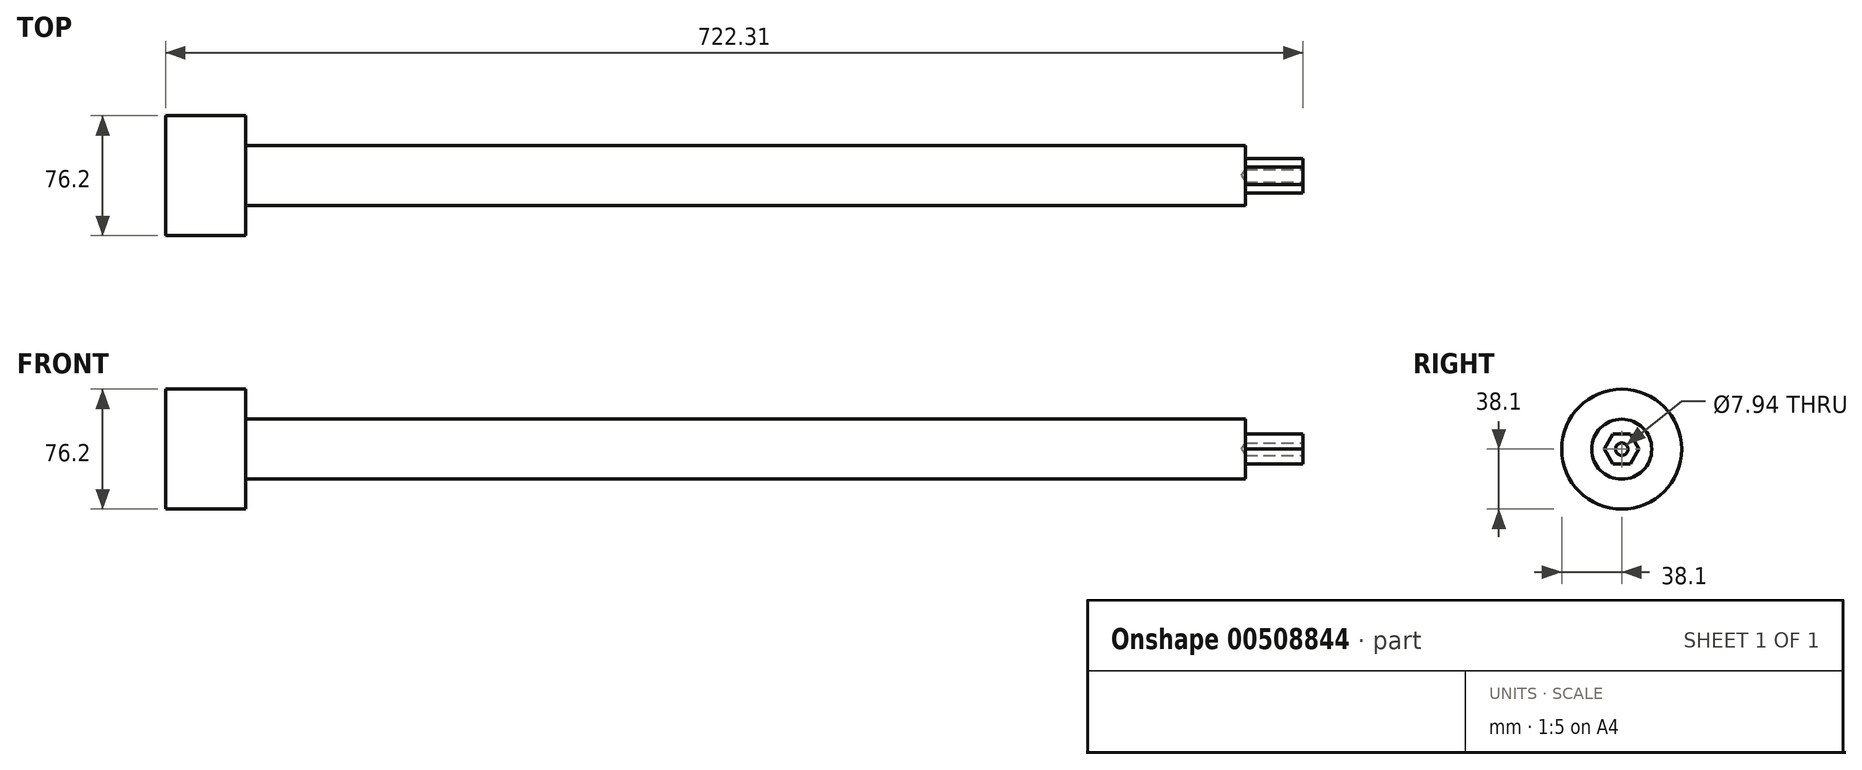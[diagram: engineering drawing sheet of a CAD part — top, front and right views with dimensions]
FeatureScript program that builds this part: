
annotation { "Feature Type Name" : "Feature", "Feature Type Description" : "" }
export const myFeature = defineFeature(function(context is Context, id is Id, definition is map)
    precondition{}
    {
        {
            var Q0;
            Q0=qCreatedBy(makeId("Front.planeOp"),FACE);
            var sketch = newSketch(context, id + "F0", { "sketchPlane" : qUnion([Q0])});
            skLineSegment(sketch, "E0", {"start": v(-342.9, 0) * mm, "end": v(-342.9, 38.1) * mm});
            skLineSegment(sketch, "E1", {"start": v(-342.9, 38.1) * mm, "end": v(-292.1, 38.1) * mm});
            skLineSegment(sketch, "E2", {"start": v(-292.1, 38.1) * mm, "end": v(-292.1, 19.05) * mm});
            skLineSegment(sketch, "E3", {"start": v(-292.1, 19.05) * mm, "end": v(342.9, 19.05) * mm});
            skLineSegment(sketch, "E4", {"start": v(342.9, 19.05) * mm, "end": v(342.9, 0) * mm});
            skLineSegment(sketch, "E5", {"start": v(342.9, 0) * mm, "end": v(-342.9, 0) * mm});
            skSolve(sketch);
        }
        {
            var Q0;
            Q0=makeQuery(id+"F0.imprint","IMPRINT",FACE,{"disambiguationData":[TD([[makeQuery(id+"F0.imprint","IMPRINT",EDGE,{"derivedFrom":sQuery(id+"F0.wireOp",EDGE,"E0")}),-1.0]])]});
            var Q1;
            Q1=sQuery(id+"F0.wireOp",EDGE,"E5");
            revolve(context, id + "F1", {"entities" : qUnion([Q0]), "axis" : qUnion([Q1]), "revolveType" : RevolveType.FULL});
        }
        {
            var Q0;
            Q0=makeQuery(id+"F1.opRevolve","SWEPT_FACE",FACE,{"disambiguationData":[OSD([sQuery(id+"F0.wireOp",EDGE,"E4")])]});
            var sketch = newSketch(context, id + "F2", { "sketchPlane" : qUnion([Q0])});
            skCircle(sketch, "E6.cCircle", {"center": v(0, 0) * mm, "radius": 9.53 * mm, "construction": true});
            skLineSegment(sketch, "E6.0", {"start": v(-5.5, 9.53) * mm, "end": v(5.5, 9.53) * mm});
            skLineSegment(sketch, "E6.1", {"start": v(5.5, 9.52) * mm, "end": v(11, 0) * mm});
            skLineSegment(sketch, "E6.2", {"start": v(11, 0) * mm, "end": v(5.5, -9.52) * mm});
            skLineSegment(sketch, "E6.3", {"start": v(5.5, -9.52) * mm, "end": v(-5.5, -9.53) * mm});
            skLineSegment(sketch, "E6.4", {"start": v(-5.5, -9.53) * mm, "end": v(-11, 0) * mm});
            skLineSegment(sketch, "E6.5", {"start": v(-11, 0) * mm, "end": v(-5.5, 9.52) * mm});
            skPoint(sketch, "E6.0.midPoint", {"position": v(0, 9.53) * mm});
            skSolve(sketch);
        }
        {
            var Q0;
            Q0=makeQuery(id+"F2.imprint","IMPRINT",FACE,{"disambiguationData":[TD([[makeQuery(id+"F2.imprint","IMPRINT",EDGE,{"derivedFrom":sQuery(id+"F2.wireOp",EDGE,"E6.0")}),-1.0]])]});
            extrude(context, id + "F3", {"entities" : qUnion([Q0]), "operationType" : NewBodyOperationType.ADD, "depth" : 36.5 * mm});
        }
        {
            var Q0;
            Q0=makeQuery(id+"F3.opExtrude","CAP_FACE",FACE,{"disambiguationData":[OSD([sQuery(id+"F2.wireOp",EDGE,"E6.0"),sQuery(id+"F2.wireOp",EDGE,"E6.1"),sQuery(id+"F2.wireOp",EDGE,"E6.2"),sQuery(id+"F2.wireOp",EDGE,"E6.3"),sQuery(id+"F2.wireOp",EDGE,"E6.4"),sQuery(id+"F2.wireOp",EDGE,"E6.5")])],"isStart":false});
            var sketch = newSketch(context, id + "F4", { "sketchPlane" : qUnion([Q0])});
            skPoint(sketch, "E7", {"position": v(0, 0) * mm});
            skSolve(sketch);
        }
        {
            var Q0;
            Q0=sQuery(id+"F4.wireOp",VERTEX,"E7");
            var Q1;
            Q1=makeQuery(id+"F1.opRevolve","SWEPT_BODY",BODY,{"disambiguationData":[OSD([sQuery(id+"F0.wireOp",EDGE,"E0"),sQuery(id+"F0.wireOp",EDGE,"E1"),sQuery(id+"F0.wireOp",EDGE,"E2"),sQuery(id+"F0.wireOp",EDGE,"E3"),sQuery(id+"F0.wireOp",EDGE,"E4"),sQuery(id+"F0.wireOp",EDGE,"E5")])]});
            hole(context, id + "F5", {"style" : HoleStyle.SIMPLE, "endStyle" : HoleEndStyle.BLIND, "standardTappedOrClearance" : lookupTablePath({ "standard" : "ANSI", "engagement" : "75%", "pitch" : "16 tpi", "size" : "3/8", "type" : "Tapped" }), "standardBlindInLast" : lookupTablePath({ "standard" : "ANSI", "engagement" : "75%", "pitch" : "16 tpi", "size" : "3/8", "type" : "Tapped" }), "holeDiameter" : 7.94 * mm, "showTappedDepth" : true, "holeDepth" : 36.5 * mm, "isTappedThrough" : true, "tappedDepth" : 31.75 * mm, "tapClearance" : 3, "locations" : qUnion([Q0]), "scope" : qUnion([Q1]), "majorDiameter" : 9.53 * mm});
        }
    });
